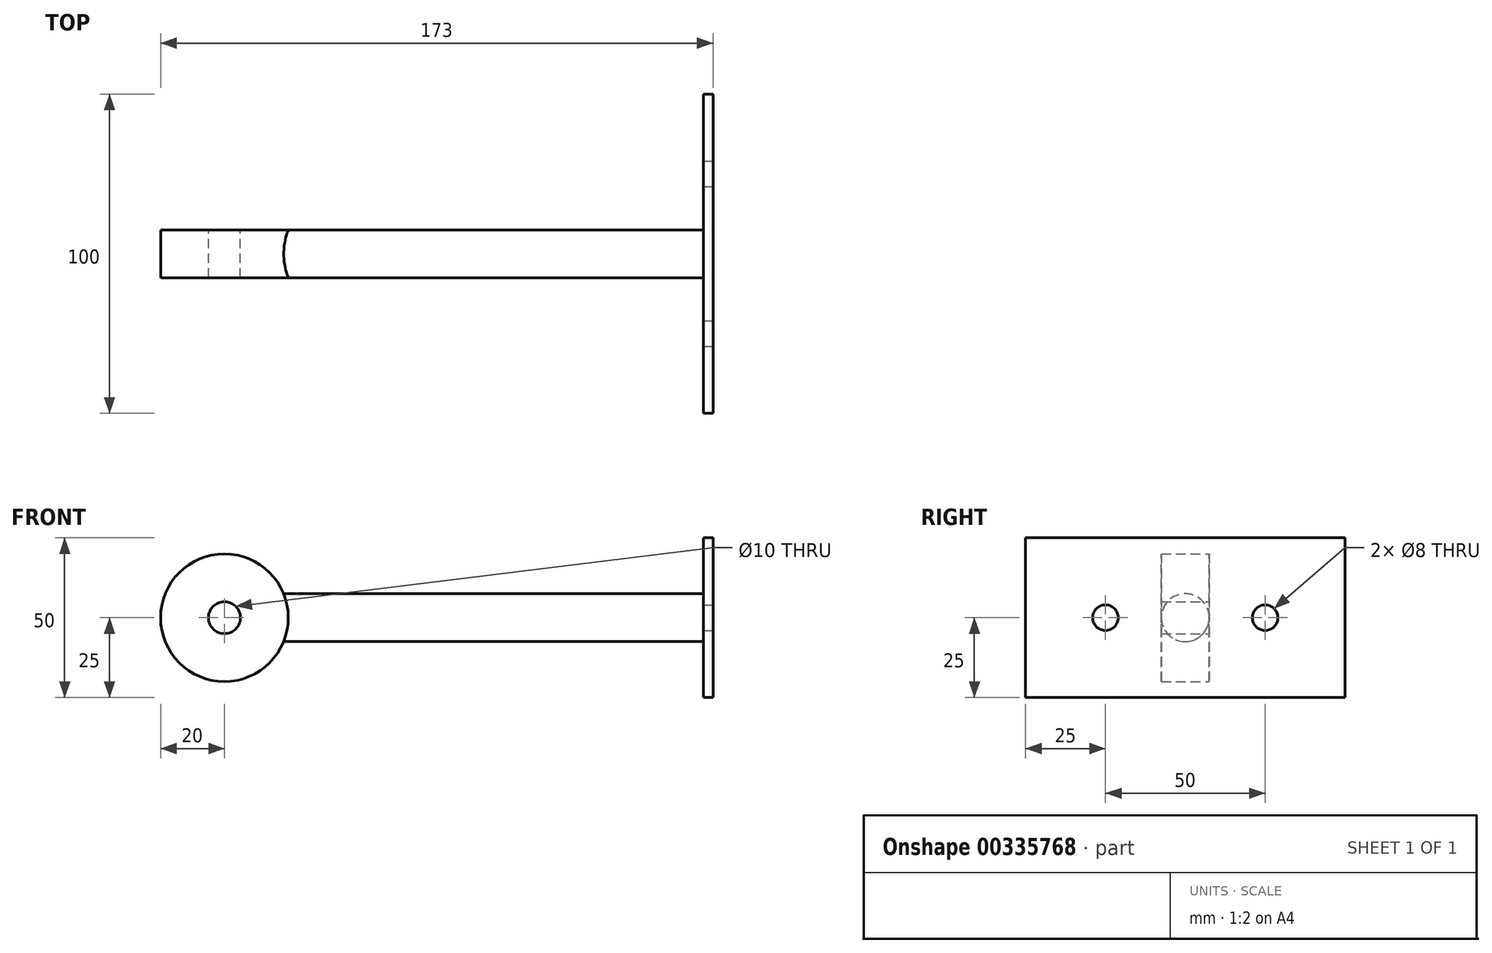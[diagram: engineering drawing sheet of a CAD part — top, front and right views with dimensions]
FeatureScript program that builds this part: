
annotation { "Feature Type Name" : "Feature", "Feature Type Description" : "" }
export const myFeature = defineFeature(function(context is Context, id is Id, definition is map)
    precondition{}
    {
        {
            var Q0;
            Q0=qCreatedBy(makeId("Front.planeOp"),FACE);
            var sketch = newSketch(context, id + "F0", { "sketchPlane" : qUnion([Q0])});
            skCircle(sketch, "E0", {"center": v(0, 0) * mm, "radius": 20 * mm});
            skCircle(sketch, "E1", {"center": v(0, 0) * mm, "radius": 5 * mm});
            skSolve(sketch);
        }
        {
            var Q0;
            Q0=makeQuery(id+"F0.imprint","IMPRINT",FACE,{"disambiguationData":[TD([[makeQuery(id+"F0.imprint","IMPRINT",EDGE,{"derivedFrom":sQuery(id+"F0.wireOp",EDGE,"E0")}),1.0]])]});
            extrude(context, id + "F1", {"entities" : qUnion([Q0]), "depth" : 15 * mm, "symmetric" : true});
        }
        {
            var Q0;
            Q0=qCreatedBy(makeId("Right.planeOp"),FACE);
            cPlane(context, id + "F2", {"entities" : qUnion([Q0]), "cplaneType" : CPlaneType.OFFSET, "offset" : 150 * mm, "width" : 150 * mm, "height" : 150 * mm});
        }
        {
            var Q0;
            Q0=qCreatedBy(id+"F2.planeOp",FACE);
            var sketch = newSketch(context, id + "F3", { "sketchPlane" : qUnion([Q0])});
            skCircle(sketch, "E2", {"center": v(0, 0) * mm, "radius": 7.5 * mm});
            skSolve(sketch);
        }
        {
            var Q0;
            Q0=makeQuery(id+"F3.imprint","IMPRINT",FACE,{"disambiguationData":[TD([[makeQuery(id+"F3.imprint","IMPRINT",EDGE,{"derivedFrom":sQuery(id+"F3.wireOp",EDGE,"E2")}),1.0]])]});
            extrude(context, id + "F4", {"entities" : qUnion([Q0]), "operationType" : NewBodyOperationType.ADD, "endBound" : BoundingType.UP_TO_NEXT, "oppositeDirection" : true, "depth" : 25 * mm});
        }
        {
            var Q0;
            Q0=qCreatedBy(id+"F2.planeOp",FACE);
            var sketch = newSketch(context, id + "F5", { "sketchPlane" : qUnion([Q0])});
            skLineSegment(sketch, "E3.bottom", {"start": v(50, 25) * mm, "end": v(-50, 25) * mm});
            skLineSegment(sketch, "E3.top", {"start": v(50, -25) * mm, "end": v(-50, -25) * mm});
            skLineSegment(sketch, "E3.left", {"start": v(50, 25) * mm, "end": v(50, -25) * mm});
            skLineSegment(sketch, "E3.right", {"start": v(-50, 25) * mm, "end": v(-50, -25) * mm});
            skPoint(sketch, "E3.middle", {"position": v(0, 0) * mm});
            skSolve(sketch);
        }
        {
            var Q0;
            Q0=makeQuery(id+"F5.imprint","IMPRINT",FACE,{"disambiguationData":[TD([[makeQuery(id+"F5.imprint","IMPRINT",EDGE,{"derivedFrom":sQuery(id+"F5.wireOp",EDGE,"E3.bottom")}),1.0]])]});
            extrude(context, id + "F6", {"entities" : qUnion([Q0]), "operationType" : NewBodyOperationType.ADD, "depth" : 3 * mm});
        }
        {
            var Q0;
            Q0=makeQuery(id+"F6.opExtrude","CAP_FACE",FACE,{"disambiguationData":[OSD([sQuery(id+"F5.wireOp",EDGE,"E3.bottom"),sQuery(id+"F5.wireOp",EDGE,"E3.top"),sQuery(id+"F5.wireOp",EDGE,"E3.left"),sQuery(id+"F5.wireOp",EDGE,"E3.right")])],"isStart":false});
            var sketch = newSketch(context, id + "F7", { "sketchPlane" : qUnion([Q0])});
            skCircle(sketch, "E4", {"center": v(-25, 0) * mm, "radius": 4 * mm});
            skCircle(sketch, "E5", {"center": v(25, 0) * mm, "radius": 4 * mm});
            skLineSegment(sketch, "E6", {"start": v(-25, 0) * mm, "end": v(25, 0) * mm, "construction": true});
            skSolve(sketch);
        }
        {
            var Q0;
            Q0 = qSketchRegion(id + "F7", true);
            extrude(context, id + "F8", {"entities" : qUnion([Q0]), "operationType" : NewBodyOperationType.REMOVE, "endBound" : BoundingType.UP_TO_NEXT, "oppositeDirection" : true, "depth" : 25 * mm});
        }
    });
